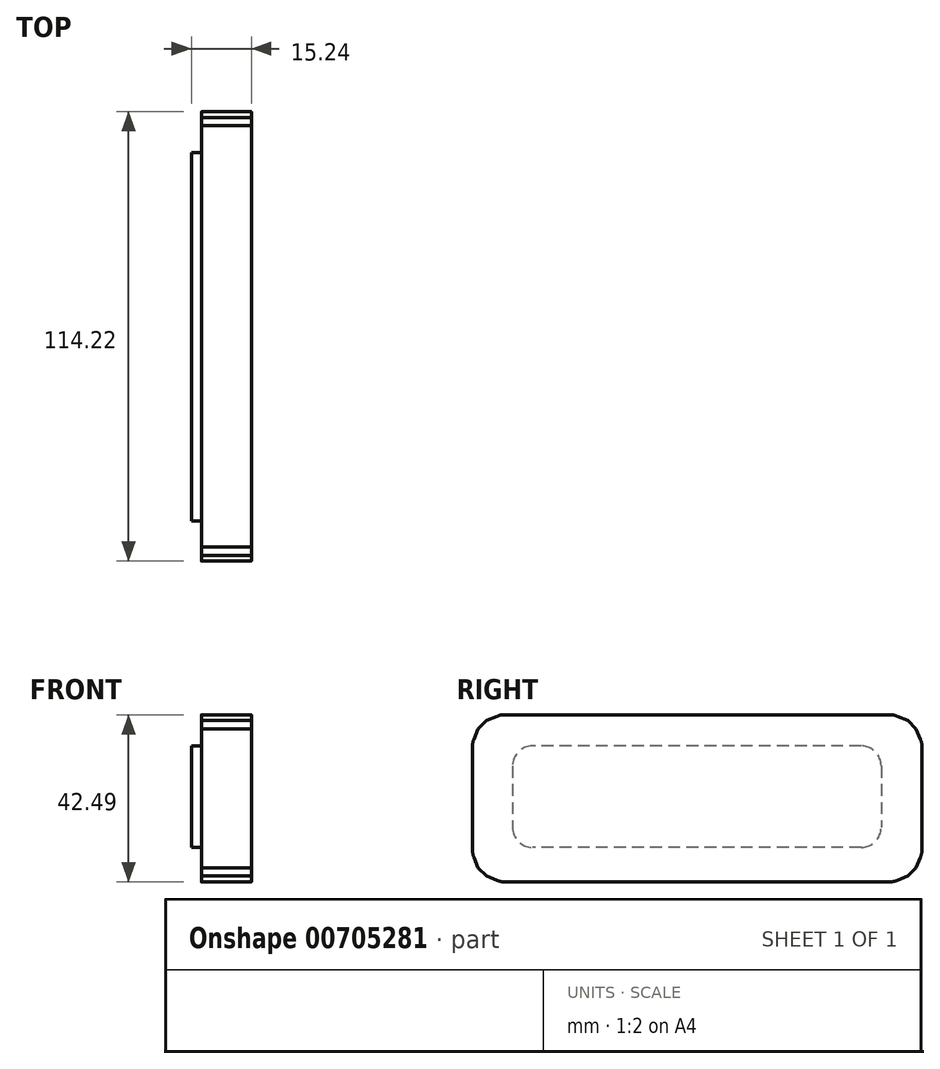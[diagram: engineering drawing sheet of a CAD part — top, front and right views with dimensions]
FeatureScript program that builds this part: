
annotation { "Feature Type Name" : "Feature", "Feature Type Description" : "" }
export const myFeature = defineFeature(function(context is Context, id is Id, definition is map)
    precondition{}
    {
        {
            var Q0;
            Q0=qCreatedBy(makeId("Right.planeOp"),FACE);
            var sketch = newSketch(context, id + "F0", { "sketchPlane" : qUnion([Q0])});
            skLineSegment(sketch, "E0.bottom", {"start": v(-46.33, 23.93) * mm, "end": v(67.9, 23.93) * mm});
            skLineSegment(sketch, "E0.top", {"start": v(-46.33, -18.56) * mm, "end": v(67.9, -18.56) * mm});
            skLineSegment(sketch, "E0.left", {"start": v(-46.33, 23.93) * mm, "end": v(-46.33, -18.56) * mm});
            skLineSegment(sketch, "E0.right", {"start": v(67.9, 23.93) * mm, "end": v(67.9, -18.56) * mm});
            skSolve(sketch);
        }
        {
            var Q0;
            Q0 = qSketchRegion(id + "F0", true);
            extrude(context, id + "F1", {"entities" : qUnion([Q0]), "depth" : 12.7 * mm, "offsetDistance" : 25.4 * mm});
        }
        {
            var Q0;
            Q0=makeQuery(id+"F1.opExtrude","CAP_FACE",FACE,{"disambiguationData":[OSD([sQuery(id+"F0.wireOp",EDGE,"E0.bottom"),sQuery(id+"F0.wireOp",EDGE,"E0.top"),sQuery(id+"F0.wireOp",EDGE,"E0.left"),sQuery(id+"F0.wireOp",EDGE,"E0.right")])],"isStart":true});
            var sketch = newSketch(context, id + "F2", { "sketchPlane" : qUnion([Q0])});
            skLineSegment(sketch, "E1.bottom", {"start": v(-57.53, 15.97) * mm, "end": v(36.13, 15.97) * mm});
            skLineSegment(sketch, "E1.top", {"start": v(-57.53, -9.77) * mm, "end": v(36.13, -9.77) * mm});
            skLineSegment(sketch, "E1.left", {"start": v(-57.53, 15.97) * mm, "end": v(-57.53, -9.77) * mm});
            skLineSegment(sketch, "E1.right", {"start": v(36.13, 15.97) * mm, "end": v(36.13, -9.77) * mm});
            skSolve(sketch);
        }
        {
            var Q0;
            Q0 = qSketchRegion(id + "F2", true);
            extrude(context, id + "F3", {"entities" : qUnion([Q0]), "operationType" : NewBodyOperationType.ADD, "depth" : 2.54 * mm, "offsetDistance" : 25.4 * mm});
        }
        {
            var Q0;
            Q0=makeQuery(id+"F3.opExtrude","SWEPT_EDGE",EDGE,{"disambiguationData":[OSD([sQuery(id+"F2.wireOp",EDGE,"E1.bottom"),sQuery(id+"F2.wireOp",EDGE,"E1.left")])]});
            var Q1;
            Q1=makeQuery(id+"F3.opExtrude","SWEPT_EDGE",EDGE,{"disambiguationData":[OSD([sQuery(id+"F2.wireOp",EDGE,"E1.top"),sQuery(id+"F2.wireOp",EDGE,"E1.left")])]});
            var Q2;
            Q2=makeQuery(id+"F3.opExtrude","SWEPT_EDGE",EDGE,{"disambiguationData":[OSD([sQuery(id+"F2.wireOp",EDGE,"E1.top"),sQuery(id+"F2.wireOp",EDGE,"E1.right")])]});
            var Q3;
            Q3=makeQuery(id+"F3.opExtrude","SWEPT_EDGE",EDGE,{"disambiguationData":[OSD([sQuery(id+"F2.wireOp",EDGE,"E1.bottom"),sQuery(id+"F2.wireOp",EDGE,"E1.right")])]});
            fillet(context, id + "F4", {"entities" : qUnion([Q0, Q1, Q2, Q3]), "radius" : 5.08 * mm, "tangentPropagation" : true, "allowEdgeOverflow" : false});
        }
        {
            var Q0;
            Q0=makeQuery(id+"F1.opExtrude","SWEPT_EDGE",EDGE,{"disambiguationData":[OSD([sQuery(id+"F0.wireOp",EDGE,"E0.bottom"),sQuery(id+"F0.wireOp",EDGE,"E0.right")])]});
            var Q1;
            Q1=makeQuery(id+"F1.opExtrude","SWEPT_EDGE",EDGE,{"disambiguationData":[OSD([sQuery(id+"F0.wireOp",EDGE,"E0.bottom"),sQuery(id+"F0.wireOp",EDGE,"E0.left")])]});
            var Q2;
            Q2=makeQuery(id+"F1.opExtrude","SWEPT_EDGE",EDGE,{"disambiguationData":[OSD([sQuery(id+"F0.wireOp",EDGE,"E0.top"),sQuery(id+"F0.wireOp",EDGE,"E0.right")])]});
            var Q3;
            Q3=makeQuery(id+"F1.opExtrude","SWEPT_EDGE",EDGE,{"disambiguationData":[OSD([sQuery(id+"F0.wireOp",EDGE,"E0.top"),sQuery(id+"F0.wireOp",EDGE,"E0.left")])]});
            chamfer(context, id + "F5", {"entities" : qUnion([Q0, Q1, Q2, Q3]), "width" : 5.08 * mm, "tangentPropagation" : true});
        }
        {
            var Q0;
            {var subQ0=sQuery(id+"F0.wireOp",EDGE,"E0.right");Q0=makeQuery(id+"F5.opChamfer","BLEND_EDGE",EDGE,{"blendedFrom":[makeQuery(id+"F1.opExtrude","SWEPT_EDGE",EDGE,{"disambiguationData":[OSD([sQuery(id+"F0.wireOp",EDGE,"E0.bottom"),subQ0])]}),makeQuery(id+"F1.opExtrude","SWEPT_FACE",FACE,{"disambiguationData":[OSD([subQ0])]})],"blendedInto":[makeQuery(id+"F1.opExtrude","SWEPT_FACE",FACE,{"disambiguationData":[OSD([subQ0])]})]});}
            var Q1;
            {var subQ0=sQuery(id+"F0.wireOp",EDGE,"E0.bottom");Q1=makeQuery(id+"F5.opChamfer","BLEND_EDGE",EDGE,{"blendedFrom":[makeQuery(id+"F1.opExtrude","SWEPT_EDGE",EDGE,{"disambiguationData":[OSD([subQ0,sQuery(id+"F0.wireOp",EDGE,"E0.right")])]}),makeQuery(id+"F1.opExtrude","SWEPT_FACE",FACE,{"disambiguationData":[OSD([subQ0])]})],"blendedInto":[makeQuery(id+"F1.opExtrude","SWEPT_FACE",FACE,{"disambiguationData":[OSD([subQ0])]})]});}
            var Q2;
            {var subQ0=sQuery(id+"F0.wireOp",EDGE,"E0.top");Q2=makeQuery(id+"F5.opChamfer","BLEND_EDGE",EDGE,{"blendedFrom":[makeQuery(id+"F1.opExtrude","SWEPT_EDGE",EDGE,{"disambiguationData":[OSD([subQ0,sQuery(id+"F0.wireOp",EDGE,"E0.right")])]}),makeQuery(id+"F1.opExtrude","SWEPT_FACE",FACE,{"disambiguationData":[OSD([subQ0])]})],"blendedInto":[makeQuery(id+"F1.opExtrude","SWEPT_FACE",FACE,{"disambiguationData":[OSD([subQ0])]})]});}
            var Q3;
            {var subQ0=sQuery(id+"F0.wireOp",EDGE,"E0.right");Q3=makeQuery(id+"F5.opChamfer","BLEND_EDGE",EDGE,{"blendedFrom":[makeQuery(id+"F1.opExtrude","SWEPT_EDGE",EDGE,{"disambiguationData":[OSD([sQuery(id+"F0.wireOp",EDGE,"E0.top"),subQ0])]}),makeQuery(id+"F1.opExtrude","SWEPT_FACE",FACE,{"disambiguationData":[OSD([subQ0])]})],"blendedInto":[makeQuery(id+"F1.opExtrude","SWEPT_FACE",FACE,{"disambiguationData":[OSD([subQ0])]})]});}
            var Q4;
            {var subQ0=sQuery(id+"F0.wireOp",EDGE,"E0.top");Q4=makeQuery(id+"F5.opChamfer","BLEND_EDGE",EDGE,{"blendedFrom":[makeQuery(id+"F1.opExtrude","SWEPT_EDGE",EDGE,{"disambiguationData":[OSD([subQ0,sQuery(id+"F0.wireOp",EDGE,"E0.left")])]}),makeQuery(id+"F1.opExtrude","SWEPT_FACE",FACE,{"disambiguationData":[OSD([subQ0])]})],"blendedInto":[makeQuery(id+"F1.opExtrude","SWEPT_FACE",FACE,{"disambiguationData":[OSD([subQ0])]})]});}
            var Q5;
            {var subQ0=sQuery(id+"F0.wireOp",EDGE,"E0.left");Q5=makeQuery(id+"F5.opChamfer","BLEND_EDGE",EDGE,{"blendedFrom":[makeQuery(id+"F1.opExtrude","SWEPT_EDGE",EDGE,{"disambiguationData":[OSD([sQuery(id+"F0.wireOp",EDGE,"E0.top"),subQ0])]}),makeQuery(id+"F1.opExtrude","SWEPT_FACE",FACE,{"disambiguationData":[OSD([subQ0])]})],"blendedInto":[makeQuery(id+"F1.opExtrude","SWEPT_FACE",FACE,{"disambiguationData":[OSD([subQ0])]})]});}
            var Q6;
            {var subQ0=sQuery(id+"F0.wireOp",EDGE,"E0.left");Q6=makeQuery(id+"F5.opChamfer","BLEND_EDGE",EDGE,{"blendedFrom":[makeQuery(id+"F1.opExtrude","SWEPT_EDGE",EDGE,{"disambiguationData":[OSD([sQuery(id+"F0.wireOp",EDGE,"E0.bottom"),subQ0])]}),makeQuery(id+"F1.opExtrude","SWEPT_FACE",FACE,{"disambiguationData":[OSD([subQ0])]})],"blendedInto":[makeQuery(id+"F1.opExtrude","SWEPT_FACE",FACE,{"disambiguationData":[OSD([subQ0])]})]});}
            var Q7;
            {var subQ0=sQuery(id+"F0.wireOp",EDGE,"E0.bottom");Q7=makeQuery(id+"F5.opChamfer","BLEND_EDGE",EDGE,{"blendedFrom":[makeQuery(id+"F1.opExtrude","SWEPT_EDGE",EDGE,{"disambiguationData":[OSD([subQ0,sQuery(id+"F0.wireOp",EDGE,"E0.left")])]}),makeQuery(id+"F1.opExtrude","SWEPT_FACE",FACE,{"disambiguationData":[OSD([subQ0])]})],"blendedInto":[makeQuery(id+"F1.opExtrude","SWEPT_FACE",FACE,{"disambiguationData":[OSD([subQ0])]})]});}
            chamfer(context, id + "F6", {"entities" : qUnion([Q0, Q1, Q2, Q3, Q4, Q5, Q6, Q7]), "width" : 5.08 * mm, "tangentPropagation" : true});
        }
        {
            var Q0;
            {var subQ0=sQuery(id+"F0.wireOp",EDGE,"E0.left");var subQ1=sQuery(id+"F0.wireOp",EDGE,"E0.top");var subQ2=makeQuery(id+"F1.opExtrude","SWEPT_EDGE",EDGE,{"disambiguationData":[OSD([subQ1,subQ0])]});Q0=makeQuery(id+"F6.opChamfer","BLEND_EDGE",EDGE,{"blendedFrom":[makeQuery(id+"F5.opChamfer","BLEND_EDGE",EDGE,{"blendedFrom":[subQ2,makeQuery(id+"F1.opExtrude","SWEPT_FACE",FACE,{"disambiguationData":[OSD([subQ1])]})],"blendedInto":[makeQuery(id+"F1.opExtrude","SWEPT_FACE",FACE,{"disambiguationData":[OSD([subQ1])]})]}),makeQuery(id+"F5.opChamfer","BLEND_EDGE",EDGE,{"blendedFrom":[subQ2,makeQuery(id+"F1.opExtrude","SWEPT_FACE",FACE,{"disambiguationData":[OSD([subQ0])]})],"blendedInto":[makeQuery(id+"F1.opExtrude","SWEPT_FACE",FACE,{"disambiguationData":[OSD([subQ0])]})]})],"blendedInto":[]});}
            var Q1;
            {var subQ0=sQuery(id+"F0.wireOp",EDGE,"E0.left");var subQ1=makeQuery(id+"F1.opExtrude","SWEPT_FACE",FACE,{"disambiguationData":[OSD([subQ0])]});Q1=makeQuery(id+"F6.opChamfer","BLEND_EDGE",EDGE,{"blendedFrom":[makeQuery(id+"F5.opChamfer","BLEND_EDGE",EDGE,{"blendedFrom":[makeQuery(id+"F1.opExtrude","SWEPT_EDGE",EDGE,{"disambiguationData":[OSD([sQuery(id+"F0.wireOp",EDGE,"E0.top"),subQ0])]}),subQ1],"blendedInto":[subQ1]}),subQ1],"blendedInto":[subQ1]});}
            var Q2;
            {var subQ0=sQuery(id+"F0.wireOp",EDGE,"E0.top");var subQ1=makeQuery(id+"F1.opExtrude","SWEPT_FACE",FACE,{"disambiguationData":[OSD([subQ0])]});Q2=makeQuery(id+"F6.opChamfer","BLEND_EDGE",EDGE,{"blendedFrom":[makeQuery(id+"F5.opChamfer","BLEND_EDGE",EDGE,{"blendedFrom":[makeQuery(id+"F1.opExtrude","SWEPT_EDGE",EDGE,{"disambiguationData":[OSD([subQ0,sQuery(id+"F0.wireOp",EDGE,"E0.left")])]}),subQ1],"blendedInto":[subQ1]}),subQ1],"blendedInto":[subQ1]});}
            var Q3;
            {var subQ0=sQuery(id+"F0.wireOp",EDGE,"E0.left");var subQ1=makeQuery(id+"F1.opExtrude","SWEPT_FACE",FACE,{"disambiguationData":[OSD([subQ0])]});Q3=makeQuery(id+"F6.opChamfer","BLEND_EDGE",EDGE,{"blendedFrom":[makeQuery(id+"F5.opChamfer","BLEND_EDGE",EDGE,{"blendedFrom":[makeQuery(id+"F1.opExtrude","SWEPT_EDGE",EDGE,{"disambiguationData":[OSD([sQuery(id+"F0.wireOp",EDGE,"E0.bottom"),subQ0])]}),subQ1],"blendedInto":[subQ1]}),subQ1],"blendedInto":[subQ1]});}
            var Q4;
            {var subQ0=sQuery(id+"F0.wireOp",EDGE,"E0.left");var subQ1=sQuery(id+"F0.wireOp",EDGE,"E0.bottom");var subQ2=makeQuery(id+"F1.opExtrude","SWEPT_EDGE",EDGE,{"disambiguationData":[OSD([subQ1,subQ0])]});Q4=makeQuery(id+"F6.opChamfer","BLEND_EDGE",EDGE,{"blendedFrom":[makeQuery(id+"F5.opChamfer","BLEND_EDGE",EDGE,{"blendedFrom":[subQ2,makeQuery(id+"F1.opExtrude","SWEPT_FACE",FACE,{"disambiguationData":[OSD([subQ1])]})],"blendedInto":[makeQuery(id+"F1.opExtrude","SWEPT_FACE",FACE,{"disambiguationData":[OSD([subQ1])]})]}),makeQuery(id+"F5.opChamfer","BLEND_EDGE",EDGE,{"blendedFrom":[subQ2,makeQuery(id+"F1.opExtrude","SWEPT_FACE",FACE,{"disambiguationData":[OSD([subQ0])]})],"blendedInto":[makeQuery(id+"F1.opExtrude","SWEPT_FACE",FACE,{"disambiguationData":[OSD([subQ0])]})]})],"blendedInto":[]});}
            var Q5;
            {var subQ0=sQuery(id+"F0.wireOp",EDGE,"E0.bottom");var subQ1=makeQuery(id+"F1.opExtrude","SWEPT_FACE",FACE,{"disambiguationData":[OSD([subQ0])]});Q5=makeQuery(id+"F6.opChamfer","BLEND_EDGE",EDGE,{"blendedFrom":[makeQuery(id+"F5.opChamfer","BLEND_EDGE",EDGE,{"blendedFrom":[makeQuery(id+"F1.opExtrude","SWEPT_EDGE",EDGE,{"disambiguationData":[OSD([subQ0,sQuery(id+"F0.wireOp",EDGE,"E0.left")])]}),subQ1],"blendedInto":[subQ1]}),subQ1],"blendedInto":[subQ1]});}
            var Q6;
            {var subQ0=sQuery(id+"F0.wireOp",EDGE,"E0.bottom");var subQ1=makeQuery(id+"F1.opExtrude","SWEPT_FACE",FACE,{"disambiguationData":[OSD([subQ0])]});Q6=makeQuery(id+"F6.opChamfer","BLEND_EDGE",EDGE,{"blendedFrom":[makeQuery(id+"F5.opChamfer","BLEND_EDGE",EDGE,{"blendedFrom":[makeQuery(id+"F1.opExtrude","SWEPT_EDGE",EDGE,{"disambiguationData":[OSD([subQ0,sQuery(id+"F0.wireOp",EDGE,"E0.right")])]}),subQ1],"blendedInto":[subQ1]}),subQ1],"blendedInto":[subQ1]});}
            var Q7;
            {var subQ0=sQuery(id+"F0.wireOp",EDGE,"E0.right");var subQ1=sQuery(id+"F0.wireOp",EDGE,"E0.bottom");var subQ2=makeQuery(id+"F1.opExtrude","SWEPT_EDGE",EDGE,{"disambiguationData":[OSD([subQ1,subQ0])]});Q7=makeQuery(id+"F6.opChamfer","BLEND_EDGE",EDGE,{"blendedFrom":[makeQuery(id+"F5.opChamfer","BLEND_EDGE",EDGE,{"blendedFrom":[subQ2,makeQuery(id+"F1.opExtrude","SWEPT_FACE",FACE,{"disambiguationData":[OSD([subQ1])]})],"blendedInto":[makeQuery(id+"F1.opExtrude","SWEPT_FACE",FACE,{"disambiguationData":[OSD([subQ1])]})]}),makeQuery(id+"F5.opChamfer","BLEND_EDGE",EDGE,{"blendedFrom":[subQ2,makeQuery(id+"F1.opExtrude","SWEPT_FACE",FACE,{"disambiguationData":[OSD([subQ0])]})],"blendedInto":[makeQuery(id+"F1.opExtrude","SWEPT_FACE",FACE,{"disambiguationData":[OSD([subQ0])]})]})],"blendedInto":[]});}
            var Q8;
            {var subQ0=sQuery(id+"F0.wireOp",EDGE,"E0.right");var subQ1=makeQuery(id+"F1.opExtrude","SWEPT_FACE",FACE,{"disambiguationData":[OSD([subQ0])]});Q8=makeQuery(id+"F6.opChamfer","BLEND_EDGE",EDGE,{"blendedFrom":[makeQuery(id+"F5.opChamfer","BLEND_EDGE",EDGE,{"blendedFrom":[makeQuery(id+"F1.opExtrude","SWEPT_EDGE",EDGE,{"disambiguationData":[OSD([sQuery(id+"F0.wireOp",EDGE,"E0.bottom"),subQ0])]}),subQ1],"blendedInto":[subQ1]}),subQ1],"blendedInto":[subQ1]});}
            var Q9;
            {var subQ0=sQuery(id+"F0.wireOp",EDGE,"E0.right");var subQ1=makeQuery(id+"F1.opExtrude","SWEPT_FACE",FACE,{"disambiguationData":[OSD([subQ0])]});Q9=makeQuery(id+"F6.opChamfer","BLEND_EDGE",EDGE,{"blendedFrom":[makeQuery(id+"F5.opChamfer","BLEND_EDGE",EDGE,{"blendedFrom":[makeQuery(id+"F1.opExtrude","SWEPT_EDGE",EDGE,{"disambiguationData":[OSD([sQuery(id+"F0.wireOp",EDGE,"E0.top"),subQ0])]}),subQ1],"blendedInto":[subQ1]}),subQ1],"blendedInto":[subQ1]});}
            var Q10;
            {var subQ0=sQuery(id+"F0.wireOp",EDGE,"E0.right");var subQ1=sQuery(id+"F0.wireOp",EDGE,"E0.top");var subQ2=makeQuery(id+"F1.opExtrude","SWEPT_EDGE",EDGE,{"disambiguationData":[OSD([subQ1,subQ0])]});Q10=makeQuery(id+"F6.opChamfer","BLEND_EDGE",EDGE,{"blendedFrom":[makeQuery(id+"F5.opChamfer","BLEND_EDGE",EDGE,{"blendedFrom":[subQ2,makeQuery(id+"F1.opExtrude","SWEPT_FACE",FACE,{"disambiguationData":[OSD([subQ1])]})],"blendedInto":[makeQuery(id+"F1.opExtrude","SWEPT_FACE",FACE,{"disambiguationData":[OSD([subQ1])]})]}),makeQuery(id+"F5.opChamfer","BLEND_EDGE",EDGE,{"blendedFrom":[subQ2,makeQuery(id+"F1.opExtrude","SWEPT_FACE",FACE,{"disambiguationData":[OSD([subQ0])]})],"blendedInto":[makeQuery(id+"F1.opExtrude","SWEPT_FACE",FACE,{"disambiguationData":[OSD([subQ0])]})]})],"blendedInto":[]});}
            var Q11;
            {var subQ0=sQuery(id+"F0.wireOp",EDGE,"E0.top");var subQ1=makeQuery(id+"F1.opExtrude","SWEPT_FACE",FACE,{"disambiguationData":[OSD([subQ0])]});Q11=makeQuery(id+"F6.opChamfer","BLEND_EDGE",EDGE,{"blendedFrom":[makeQuery(id+"F5.opChamfer","BLEND_EDGE",EDGE,{"blendedFrom":[makeQuery(id+"F1.opExtrude","SWEPT_EDGE",EDGE,{"disambiguationData":[OSD([subQ0,sQuery(id+"F0.wireOp",EDGE,"E0.right")])]}),subQ1],"blendedInto":[subQ1]}),subQ1],"blendedInto":[subQ1]});}
            fillet(context, id + "F7", {"entities" : qUnion([Q0, Q1, Q2, Q3, Q4, Q5, Q6, Q7, Q8, Q9, Q10, Q11]), "radius" : 5.08 * mm, "tangentPropagation" : true, "allowEdgeOverflow" : false});
        }
    });
